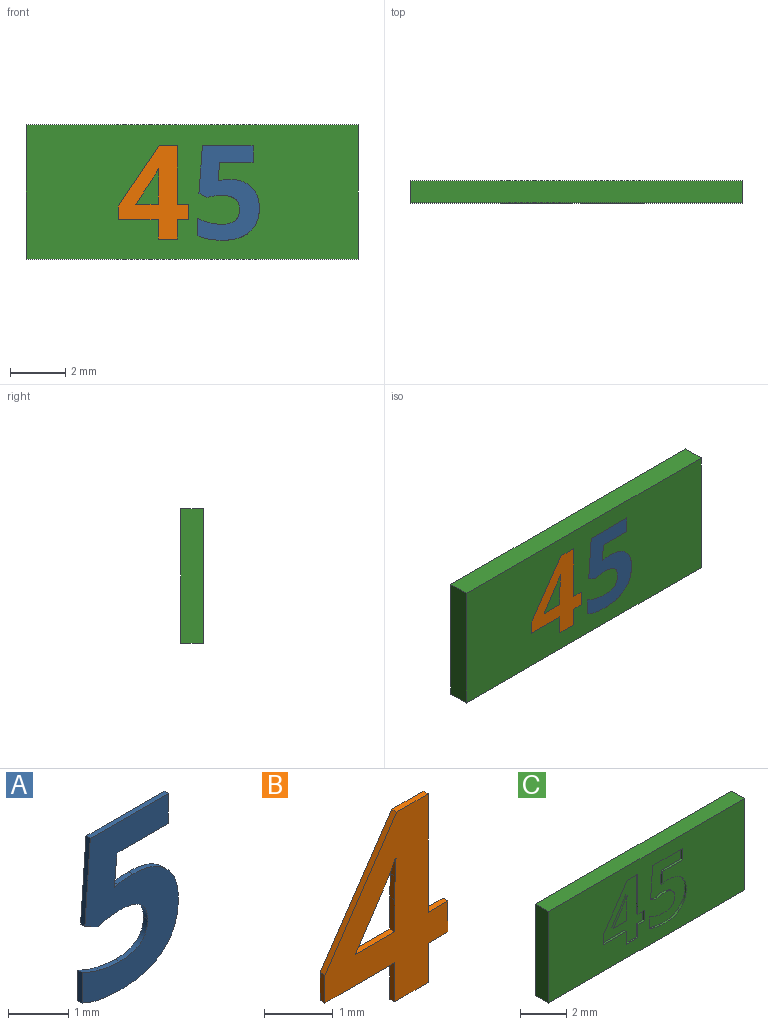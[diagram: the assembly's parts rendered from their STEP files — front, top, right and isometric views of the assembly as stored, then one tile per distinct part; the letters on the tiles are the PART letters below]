
ASSEMBLY  parts=3 mates=2
PART A: 22 faces, bbox 2.3x0.1x3.4 mm
  f0: plane 3.42x2.25mm, normal (0,-1,0), area 4.5mm2, adj f1,f2,f3,f4,f5,f6,f7,f8
  f1: plane 0.1x0.08mm, normal (-0.2,0,0.98), area 0mm2, adj f0,f2,f18,f20
  f2: plane 0.66x0.1mm, normal (1,0,-0.09), area 0.1mm2, adj f0,f1,f3,f18
  f3: plane 1.2x0.1mm, normal (0,0,-1), area 0.1mm2, adj f0,f2,f4,f18
  f4: plane 0.6x0.1mm, normal (1,0,0), area 0.1mm2, adj f0,f3,f5,f18
  f5: plane 1.83x0.1mm, normal (0,0,1), area 0.2mm2, adj f0,f4,f6,f18
  f6: plane 1.72x0.13mm, normal (-1,0,0.07), area 0.2mm2, adj f0,f5,f7,f18
  f7: plane 0.28x0.15mm, normal (-0.47,0,-0.88), area 0mm2, adj f0,f6,f8,f18
  f8: extruded ~0.24x0.1mm, area 0mm2, adj f0,f7,f9,f18
  f9: extruded ~0.27x0.1mm, area 0mm2, adj f0,f8,f10,f18
  f10: extruded ~0.68x0.51mm, area 0.1mm2, adj f0,f9,f11,f18
  f11: extruded ~0.65x0.54mm, area 0.1mm2, adj f0,f10,f12,f18
  f12: extruded ~0.46x0.1mm, area 0mm2, adj f0,f11,f13,f18
  f13: extruded ~0.42x0.16mm, area 0mm2, adj f0,f12,f14,f18
  f14: plane 0.62x0.1mm, normal (-1,0,0), area 0.1mm2, adj f0,f13,f15,f18
  f15: extruded ~0.91x0.18mm, area 0.1mm2, adj f0,f14,f16,f18
  f16: extruded ~1x0.3mm, area 0.1mm2, adj f0,f15,f17,f18
  f17: extruded ~0.87x0.35mm, area 0.1mm2, adj f0,f16,f18,f19
  f18: plane 3.42x2.25mm, normal (0,1,0), area 4.5mm2, adj f1,f2,f3,f4,f5,f6,f7,f8
  f19: extruded ~0.75x0.29mm, area 0.1mm2, adj f0,f17,f18,f21
  f20: extruded ~0.35x0.1mm, area 0mm2, adj f0,f1,f18,f21
  f21: extruded ~0.78x0.27mm, area 0.1mm2, adj f0,f18,f19,f20
PART B: 20 faces, bbox 2.5x0.1x3.4 mm
  f0: plane 3.37x2.54mm, normal (0,-1,0), area 4.3mm2, adj f1,f2,f3,f4,f5,f6,f7,f8
  f1: plane 0.41x0.1mm, normal (0,0,1), area 0mm2, adj f0,f2,f13,f15
  f2: plane 2.12x0.1mm, normal (1,0,0), area 0.2mm2, adj f0,f1,f3,f13
  f3: plane 0.66x0.1mm, normal (0,0,1), area 0.1mm2, adj f0,f2,f4,f13
  f4: plane 2.18x1.48mm, normal (-0.83,0,0.56), area 0.3mm2, adj f0,f3,f5,f13
  f5: plane 0.5x0.1mm, normal (-1,0,0), area 0mm2, adj f0,f4,f6,f13
  f6: plane 1.44x0.1mm, normal (0,0,-1), area 0.1mm2, adj f0,f5,f7,f13
  f7: plane 0.7x0.1mm, normal (-1,0,0), area 0.1mm2, adj f0,f6,f8,f13
  f8: plane 0.7x0.1mm, normal (0,0,-1), area 0.1mm2, adj f0,f7,f13,f14
  f9: plane 0.93x0.62mm, normal (0.83,0,-0.55), area 0.1mm2, adj f0,f10,f13,f18
  f10: extruded ~0.37x0.21mm, area 0mm2, adj f0,f9,f11,f13
  f11: plane 0.1x0.02mm, normal (0,0,-1), area 0mm2, adj f0,f10,f12,f13
  f12: extruded ~0.32x0.1mm, area 0mm2, adj f0,f11,f13,f17
  f13: plane 3.37x2.54mm, normal (0,1,0), area 4.3mm2, adj f1,f2,f3,f4,f5,f6,f7,f8
  f14: plane 0.7x0.1mm, normal (1,0,0), area 0.1mm2, adj f0,f8,f13,f16
  f15: plane 0.55x0.1mm, normal (1,0,0), area 0.1mm2, adj f0,f1,f13,f16
  f16: plane 0.41x0.1mm, normal (0,0,-1), area 0mm2, adj f0,f13,f14,f15
  f17: extruded ~0.42x0.1mm, area 0mm2, adj f0,f12,f13,f19
  f18: plane 0.81x0.1mm, normal (0,0,1), area 0.1mm2, adj f0,f9,f13,f19
  f19: plane 0.57x0.1mm, normal (-1,0,0), area 0.1mm2, adj f0,f13,f17,f18
PART C: 47 faces, bbox 12x0.8x4.9 mm
  f0: plane 12x4.85mm, normal (0,-1,0), area 48.9mm2, adj f1,f2,f3,f4,f6,f7,f8,f9
  f1: plane 12x0.8mm, normal (0,0,-1), area 9.6mm2, adj f0,f2,f4,f5
  f2: plane 4.85x0.8mm, normal (1,0,0), area 3.9mm2, adj f0,f1,f3,f5
  f3: plane 12x0.8mm, normal (0,0,1), area 9.6mm2, adj f0,f2,f4,f5
  f4: plane 4.85x0.8mm, normal (-1,0,0), area 3.9mm2, adj f0,f1,f3,f5
  f5: plane 12x4.85mm, normal (0,1,0), area 58.2mm2, adj f1,f2,f3,f4
  f6: plane 0.55x0.1mm, normal (-1,0,0), area 0.1mm2, adj f0,f7,f23,f24
  f7: plane 0.41x0.1mm, normal (0,0,-1), area 0mm2, adj f0,f6,f8,f24
  f8: plane 2.12x0.1mm, normal (-1,0,0), area 0.2mm2, adj f0,f7,f9,f24
  f9: plane 0.66x0.1mm, normal (0,0,-1), area 0.1mm2, adj f0,f8,f10,f24
  f10: plane 2.18x1.48mm, normal (0.83,0,-0.56), area 0.3mm2, adj f0,f9,f11,f24
  f11: plane 0.5x0.1mm, normal (1,0,0), area 0mm2, adj f0,f10,f12,f24
  f12: plane 1.44x0.1mm, normal (0,0,1), area 0.1mm2, adj f0,f11,f13,f24
  f13: plane 0.7x0.1mm, normal (1,0,0), area 0.1mm2, adj f0,f12,f14,f24
  f14: plane 0.7x0.1mm, normal (0,0,1), area 0.1mm2, adj f0,f13,f15,f24
  f15: plane 0.7x0.1mm, normal (-1,0,0), area 0.1mm2, adj f0,f14,f23,f24
  f16: plane 0.81x0.1mm, normal (0,0,-1), area 0.1mm2, adj f17,f22,f24,f25
  f17: plane 0.93x0.62mm, normal (-0.83,0,0.55), area 0.1mm2, adj f16,f18,f24,f25
  f18: extruded ~0.37x0.21mm, area 0mm2, adj f17,f19,f24,f25
  f19: plane 0.1x0.02mm, normal (0,0,1), area 0mm2, adj f18,f20,f24,f25
  f20: extruded ~0.32x0.1mm, area 0mm2, adj f19,f21,f24,f25
  f21: extruded ~0.42x0.1mm, area 0mm2, adj f20,f22,f24,f25
  f22: plane 0.57x0.1mm, normal (1,0,0), area 0.1mm2, adj f16,f21,f24,f25
  f23: plane 0.41x0.1mm, normal (0,0,1), area 0mm2, adj f0,f6,f15,f24
  f24: plane 3.37x2.54mm, normal (0,-1,0), area 4.3mm2, adj f6,f7,f8,f9,f10,f11,f12,f13
  f25: plane 1.3x0.84mm, normal (0,-1,0), area 0.5mm2, adj f16,f17,f18,f19,f20,f21,f22
  f26: extruded ~0.35x0.1mm, area 0mm2, adj f0,f27,f45,f46
  f27: plane 0.1x0.08mm, normal (0.2,0,-0.98), area 0mm2, adj f0,f26,f28,f46
  f28: plane 0.66x0.1mm, normal (-1,0,0.09), area 0.1mm2, adj f0,f27,f29,f46
  f29: plane 1.2x0.1mm, normal (0,0,1), area 0.1mm2, adj f0,f28,f30,f46
  f30: plane 0.6x0.1mm, normal (-1,0,0), area 0.1mm2, adj f0,f29,f31,f46
  f31: plane 1.83x0.1mm, normal (0,0,-1), area 0.2mm2, adj f0,f30,f32,f46
  f32: plane 1.72x0.13mm, normal (1,0,-0.07), area 0.2mm2, adj f0,f31,f33,f46
  f33: plane 0.28x0.15mm, normal (0.47,0,0.88), area 0mm2, adj f0,f32,f34,f46
  f34: extruded ~0.24x0.1mm, area 0mm2, adj f0,f33,f35,f46
  f35: extruded ~0.27x0.1mm, area 0mm2, adj f0,f34,f36,f46
  f36: extruded ~0.68x0.51mm, area 0.1mm2, adj f0,f35,f37,f46
  f37: extruded ~0.65x0.54mm, area 0.1mm2, adj f0,f36,f38,f46
  f38: extruded ~0.46x0.1mm, area 0mm2, adj f0,f37,f39,f46
  f39: extruded ~0.42x0.16mm, area 0mm2, adj f0,f38,f40,f46
  f40: plane 0.62x0.1mm, normal (1,0,0), area 0.1mm2, adj f0,f39,f41,f46
  f41: extruded ~0.91x0.18mm, area 0.1mm2, adj f0,f40,f42,f46
  f42: extruded ~1x0.3mm, area 0.1mm2, adj f0,f41,f43,f46
  f43: extruded ~0.87x0.35mm, area 0.1mm2, adj f0,f42,f44,f46
  f44: extruded ~0.75x0.29mm, area 0.1mm2, adj f0,f43,f45,f46
  f45: extruded ~0.78x0.27mm, area 0.1mm2, adj f0,f26,f44,f46
  f46: plane 3.42x2.25mm, normal (0,-1,0), area 4.5mm2, adj f26,f27,f28,f29,f30,f31,f32,f33
PLACE A t=(-0.27,0.36,-0.02)mm
PLACE B t=(-2.9,0.36,-0.02)mm
PLACE C t=(-0.05,0.36,-0.02)mm
MATE fastened A.f0 <-> C.f0  axis (0,-1,0) through (0.14,-0.44,-1.58)mm
MATE fastened B.f0 <-> C.f0  axis (0,-1,0) through (-1.27,-0.44,-1.72)mm
